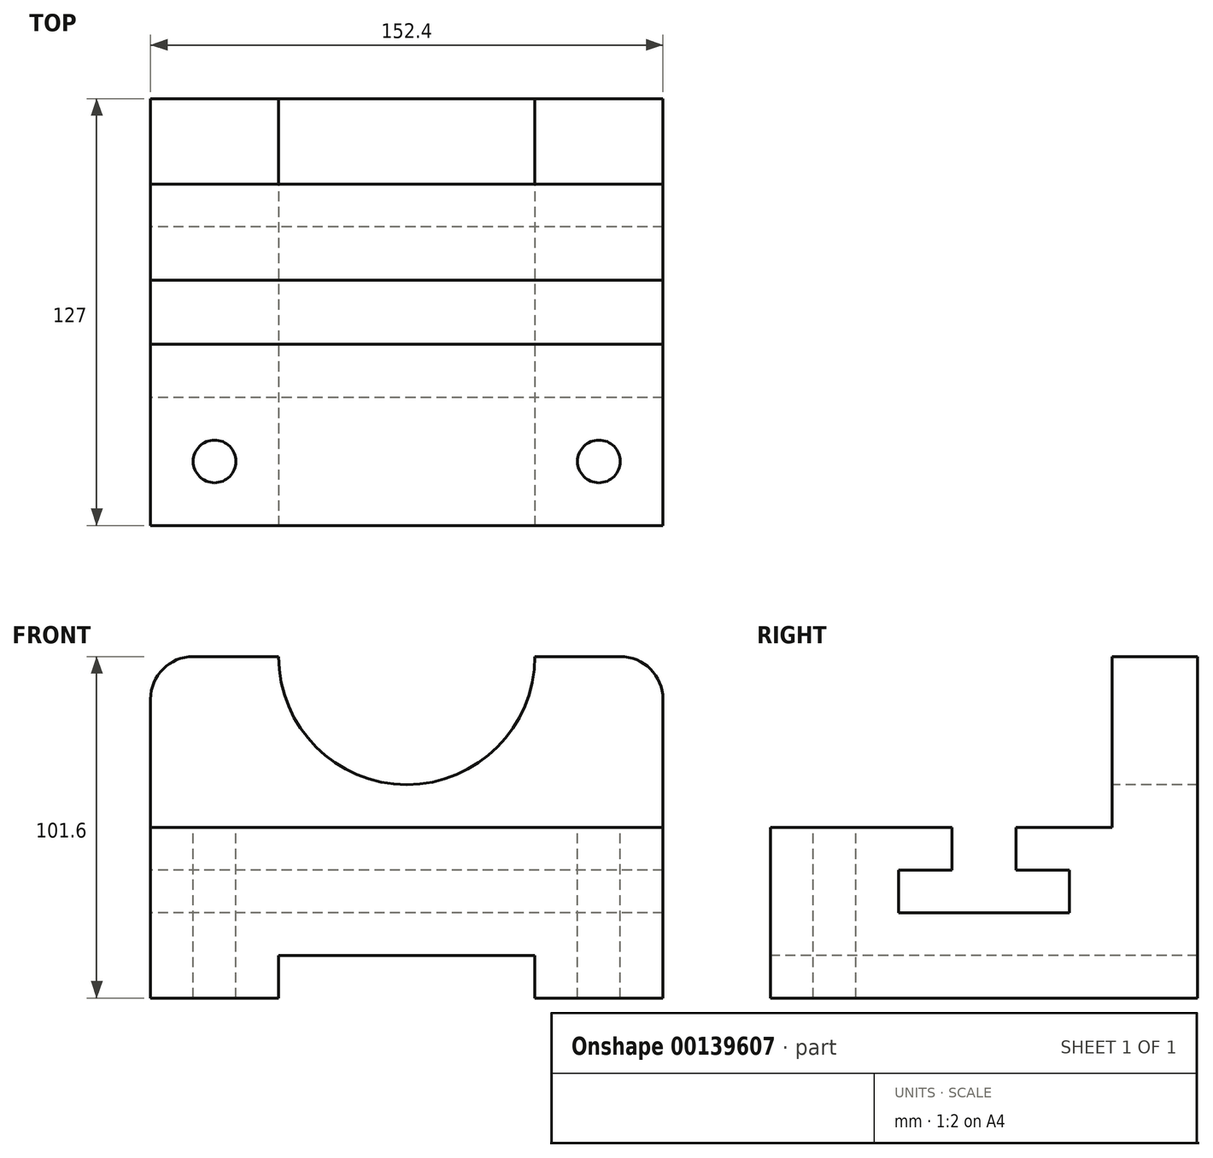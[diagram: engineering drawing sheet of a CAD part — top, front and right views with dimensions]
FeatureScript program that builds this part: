
annotation { "Feature Type Name" : "Feature", "Feature Type Description" : "" }
export const myFeature = defineFeature(function(context is Context, id is Id, definition is map)
    precondition{}
    {
        {
            var Q0;
            Q0=qCreatedBy(makeId("Right.planeOp"),FACE);
            var sketch = newSketch(context, id + "F0", { "sketchPlane" : qUnion([Q0])});
            skLineSegment(sketch, "E0", {"start": v(0, 0) * mm, "end": v(0, -50.8) * mm});
            skLineSegment(sketch, "E1", {"start": v(0, -50.8) * mm, "end": v(127, -50.8) * mm});
            skLineSegment(sketch, "E2", {"start": v(127, -50.8) * mm, "end": v(127, 50.8) * mm});
            skLineSegment(sketch, "E3", {"start": v(127, 50.8) * mm, "end": v(101.6, 50.8) * mm});
            skLineSegment(sketch, "E4", {"start": v(101.6, 50.8) * mm, "end": v(101.6, 0) * mm});
            skLineSegment(sketch, "E5", {"start": v(101.6, 0) * mm, "end": v(73.03, 0) * mm});
            skLineSegment(sketch, "E6", {"start": v(73.03, 0) * mm, "end": v(73.03, -12.7) * mm});
            skLineSegment(sketch, "E7", {"start": v(73.03, -12.7) * mm, "end": v(88.9, -12.7) * mm});
            skLineSegment(sketch, "E8", {"start": v(88.9, -12.7) * mm, "end": v(88.9, -25.4) * mm});
            skLineSegment(sketch, "E9", {"start": v(88.9, -25.4) * mm, "end": v(38.1, -25.4) * mm});
            skLineSegment(sketch, "E10", {"start": v(38.1, -25.4) * mm, "end": v(38.1, -12.7) * mm});
            skLineSegment(sketch, "E11", {"start": v(38.1, -12.7) * mm, "end": v(53.98, -12.7) * mm});
            skLineSegment(sketch, "E12", {"start": v(53.98, -12.7) * mm, "end": v(53.98, 0) * mm});
            skLineSegment(sketch, "E13", {"start": v(53.98, 0) * mm, "end": v(0, 0) * mm});
            skSolve(sketch);
        }
        {
            var Q0;
            Q0 = qSketchRegion(id + "F0", true);
            extrude(context, id + "F1", {"entities" : qUnion([Q0]), "depth" : 152.4 * mm});
        }
        {
            var Q0;
            Q0=makeQuery(id+"F1.opExtrude","CAP_EDGE",EDGE,{"disambiguationData":[OSD([sQuery(id+"F0.wireOp",EDGE,"E3")])],"isStart":false});
            var Q1;
            Q1=makeQuery(id+"F1.opExtrude","CAP_EDGE",EDGE,{"disambiguationData":[OSD([sQuery(id+"F0.wireOp",EDGE,"E3")])],"isStart":true});
            fillet(context, id + "F2", {"entities" : qUnion([Q0, Q1]), "radius" : 12.7 * mm, "tangentPropagation" : true, "allowEdgeOverflow" : false});
        }
        {
            var Q0;
            Q0=makeQuery(id+"F1.opExtrude","SWEPT_FACE",FACE,{"disambiguationData":[OSD([sQuery(id+"F0.wireOp",EDGE,"E4")])]});
            var sketch = newSketch(context, id + "F3", { "sketchPlane" : qUnion([Q0])});
            skLineSegment(sketch, "E14.0", {"start": v(139.7, 50.8) * mm, "end": v(12.7, 50.8) * mm});
            skArc(sketch, "E15.0", {"start": v(12.7, 50.8) * mm, "mid": v(3.72, 47.08) * mm, "end": v(0, 38.1) * mm});
            skLineSegment(sketch, "E16.0", {"start": v(0, 38.1) * mm, "end": v(0, 0) * mm});
            skArc(sketch, "E17.0", {"start": v(152.4, 38.1) * mm, "mid": v(148.68, 47.08) * mm, "end": v(139.7, 50.8) * mm});
            skLineSegment(sketch, "E18.0", {"start": v(152.4, 38.1) * mm, "end": v(152.4, 0) * mm});
            skPoint(sketch, "E19", {"position": v(76.2, 50.8) * mm});
            skArc(sketch, "E20", {"start": v(38.1, 50.8) * mm, "mid": v(76.2, 12.7) * mm, "end": v(114.3, 50.8) * mm});
            skSolve(sketch);
        }
        {
            var Q0;
            Q0 = qSketchRegion(id + "F3", true);
            extrude(context, id + "F4", {"entities" : qUnion([Q0]), "operationType" : NewBodyOperationType.REMOVE, "oppositeDirection" : true, "depth" : 25.4 * mm});
        }
        {
            var Q0;
            Q0=makeQuery(id+"F1.opExtrude","SWEPT_FACE",FACE,{"disambiguationData":[OSD([sQuery(id+"F0.wireOp",EDGE,"E0")])]});
            var sketch = newSketch(context, id + "F5", { "sketchPlane" : qUnion([Q0])});
            skLineSegment(sketch, "E21.0", {"start": v(0, 0) * mm, "end": v(0, -50.8) * mm});
            skLineSegment(sketch, "E22.0", {"start": v(152.4, -50.8) * mm, "end": v(0, -50.8) * mm});
            skLineSegment(sketch, "E23.0", {"start": v(152.4, 0) * mm, "end": v(152.4, -50.8) * mm});
            skLineSegment(sketch, "E24", {"start": v(38.1, -50.8) * mm, "end": v(38.1, -38.1) * mm});
            skLineSegment(sketch, "E25", {"start": v(38.1, -38.1) * mm, "end": v(114.3, -38.1) * mm});
            skLineSegment(sketch, "E26", {"start": v(114.3, -38.1) * mm, "end": v(114.3, -50.8) * mm});
            skSolve(sketch);
        }
        {
            var Q0;
            Q0 = qSketchRegion(id + "F5", true);
            extrude(context, id + "F6", {"entities" : qUnion([Q0]), "operationType" : NewBodyOperationType.REMOVE, "endBound" : BoundingType.THROUGH_ALL, "oppositeDirection" : true, "depth" : 25.4 * mm});
        }
        {
            var Q0;
            Q0=makeQuery(id+"F1.opExtrude","SWEPT_FACE",FACE,{"disambiguationData":[OSD([sQuery(id+"F0.wireOp",EDGE,"E13")])]});
            var sketch = newSketch(context, id + "F7", { "sketchPlane" : qUnion([Q0])});
            skLineSegment(sketch, "E27", {"start": v(19.05, 0) * mm, "end": v(19.05, 19.05) * mm, "construction": true});
            skLineSegment(sketch, "E28", {"start": v(133.35, 0) * mm, "end": v(133.35, 19.05) * mm, "construction": true});
            skCircle(sketch, "E29", {"center": v(19.05, 19.05) * mm, "radius": 6.35 * mm});
            skCircle(sketch, "E30", {"center": v(133.35, 19.05) * mm, "radius": 6.35 * mm});
            skSolve(sketch);
        }
        {
            var Q0;
            Q0 = qSketchRegion(id + "F7", true);
            extrude(context, id + "F8", {"entities" : qUnion([Q0]), "operationType" : NewBodyOperationType.REMOVE, "endBound" : BoundingType.THROUGH_ALL, "oppositeDirection" : true, "depth" : 25.4 * mm});
        }
    });
